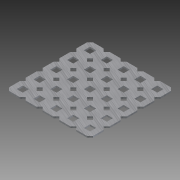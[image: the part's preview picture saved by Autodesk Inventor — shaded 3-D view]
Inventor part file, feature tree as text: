
AUTODESK INVENTOR PART (.ipt)
format: ipt  version: 2012 (Build 160160000, 160)  size: 1,805,312 bytes
history: native  units: in
note: dims shown in document units (in); Inventor stores cm internally (conversion verified against a paired STEP export)
features: other x1, imported_body x1, sketch x1, plane x1, split x1
ambient origin geometry x8: Origin, YZ Plane, XZ Plane, XY Plane, X Axis, Y Axis, Z Axis, Center Point
feature tree (5):
  parser-record x1  (decoder bookkeeping rows leaked as tree rows — omitted from the tree; the rows remain in map.json)
  imported_body  "Base1"
  sketch  "Sketch2"  dims[d6=9.8425in d8=0.5in d9=1.9685in d11=0.5in d16=-2.5in]
  plane  "Work Plane1"
  split  "Split1"
